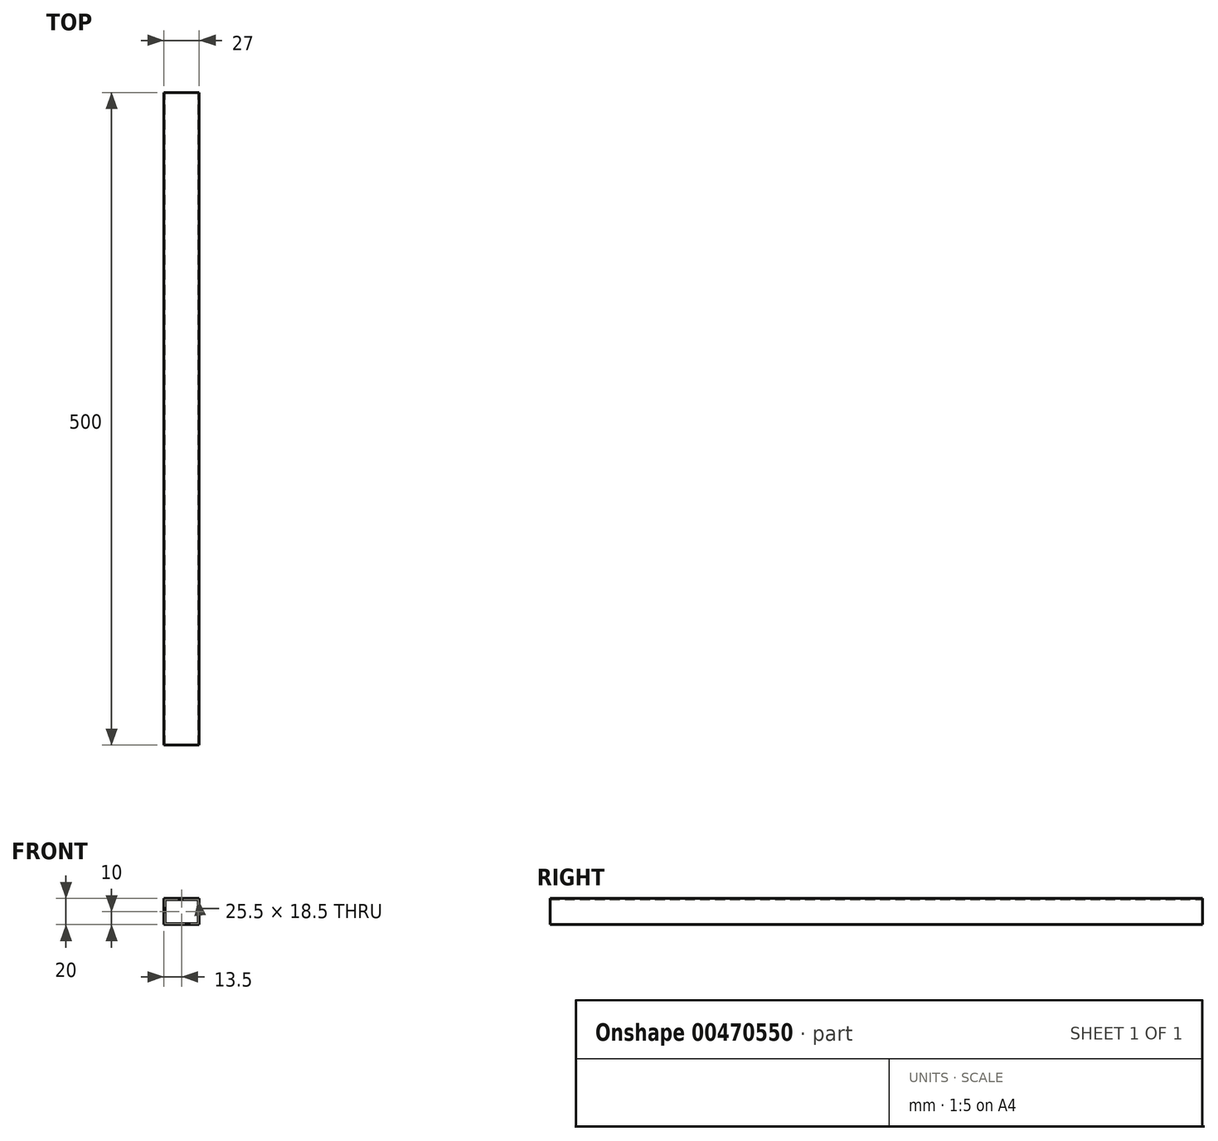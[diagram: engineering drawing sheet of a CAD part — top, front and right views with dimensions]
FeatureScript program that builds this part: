
annotation { "Feature Type Name" : "Feature", "Feature Type Description" : "" }
export const myFeature = defineFeature(function(context is Context, id is Id, definition is map)
    precondition{}
    {
        {
            assignVariable(context, id + "F0", {"name" : "TuboLargo", "anyValue" : 500 * mm});
        }
        {
            var Q0;
            Q0=qCreatedBy(makeId("Front.planeOp"),FACE);
            var sketch = newSketch(context, id + "F1", { "sketchPlane" : qUnion([Q0])});
            skLineSegment(sketch, "E0.bottom", {"start": v(13.5, -10) * mm, "end": v(-13.5, -10) * mm});
            skLineSegment(sketch, "E0.top", {"start": v(13.5, 10) * mm, "end": v(-13.5, 10) * mm});
            skLineSegment(sketch, "E0.left", {"start": v(13.5, -10) * mm, "end": v(13.5, 10) * mm});
            skLineSegment(sketch, "E0.right", {"start": v(-13.5, -10) * mm, "end": v(-13.5, 10) * mm});
            skLineSegment(sketch, "E1.bottom", {"start": v(-12.75, 9.25) * mm, "end": v(12.75, 9.25) * mm});
            skLineSegment(sketch, "E1.top", {"start": v(-12.75, -9.25) * mm, "end": v(12.75, -9.25) * mm});
            skLineSegment(sketch, "E1.left", {"start": v(-12.75, 9.25) * mm, "end": v(-12.75, -9.25) * mm});
            skLineSegment(sketch, "E1.right", {"start": v(12.75, 9.25) * mm, "end": v(12.75, -9.25) * mm});
            skPoint(sketch, "E1.middle", {"position": v(0, 0) * mm});
            skSolve(sketch);
        }
        {
            var Q0;
            Q0 = qSketchRegion(id + "F1", true);
            extrude(context, id + "F2", {"entities" : qUnion([Q0]), "depth" : (getVariable(context, 'TuboLargo'))});
        }
    });
